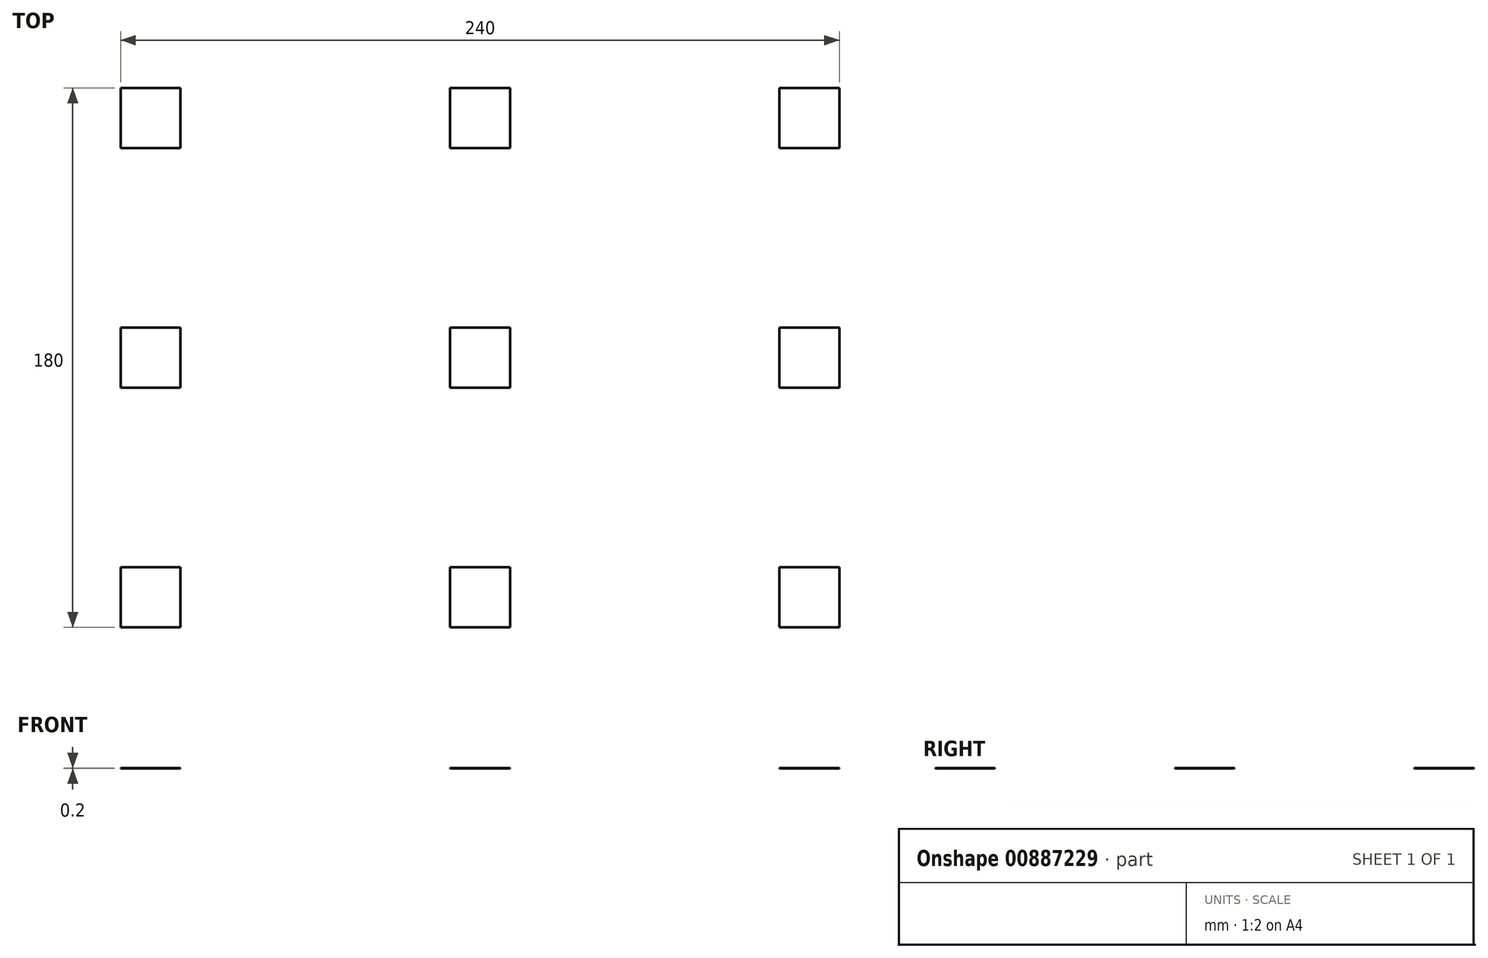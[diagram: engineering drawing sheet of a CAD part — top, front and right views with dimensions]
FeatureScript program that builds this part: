
annotation { "Feature Type Name" : "Feature", "Feature Type Description" : "" }
export const myFeature = defineFeature(function(context is Context, id is Id, definition is map)
    precondition{}
    {
        {
            var Q0;
            Q0=qCreatedBy(makeId("Top.planeOp"), FACE);
            var sketch = newSketch(context, id + "F0", { "sketchPlane" : qUnion([Q0])});
            skLineSegment(sketch, "E0.bottom", {"start": v(10, -10) * mm, "end": v(-10, -10) * mm});
            skLineSegment(sketch, "E0.top", {"start": v(10, 10) * mm, "end": v(-10, 10) * mm});
            skLineSegment(sketch, "E0.left", {"start": v(10, -10) * mm, "end": v(10, 10) * mm});
            skLineSegment(sketch, "E0.right", {"start": v(-10, -10) * mm, "end": v(-10, 10) * mm});
            skPoint(sketch, "E0.middle", {"position": v(0, 0) * mm});
            skLineSegment(sketch, "E1.0.0.1", {"start": v(10, 90) * mm, "end": v(-10, 90) * mm});
            skLineSegment(sketch, "E1.1.0.1", {"start": v(10, 70) * mm, "end": v(10, 90) * mm});
            skLineSegment(sketch, "E1.2.0.1", {"start": v(-10, 70) * mm, "end": v(-10, 90) * mm});
            skPoint(sketch, "E1.3.0.1", {"position": v(0, 80) * mm});
            skLineSegment(sketch, "E1.4.0.1", {"start": v(10, 70) * mm, "end": v(-10, 70) * mm});
            skLineSegment(sketch, "E1.0.0.2", {"start": v(10, 170) * mm, "end": v(-10, 170) * mm});
            skLineSegment(sketch, "E1.1.0.2", {"start": v(10, 150) * mm, "end": v(10, 170) * mm});
            skLineSegment(sketch, "E1.2.0.2", {"start": v(-10, 150) * mm, "end": v(-10, 170) * mm});
            skPoint(sketch, "E1.3.0.2", {"position": v(0, 160) * mm});
            skLineSegment(sketch, "E1.4.0.2", {"start": v(10, 150) * mm, "end": v(-10, 150) * mm});
            skLineSegment(sketch, "E1.0.1.0", {"start": v(120, 10) * mm, "end": v(100, 10) * mm});
            skLineSegment(sketch, "E1.1.1.0", {"start": v(120, -10) * mm, "end": v(120, 10) * mm});
            skLineSegment(sketch, "E1.2.1.0", {"start": v(100, -10) * mm, "end": v(100, 10) * mm});
            skPoint(sketch, "E1.3.1.0", {"position": v(110, 0) * mm});
            skLineSegment(sketch, "E1.4.1.0", {"start": v(120, -10) * mm, "end": v(100, -10) * mm});
            skLineSegment(sketch, "E1.0.1.1", {"start": v(120, 90) * mm, "end": v(100, 90) * mm});
            skLineSegment(sketch, "E1.1.1.1", {"start": v(120, 70) * mm, "end": v(120, 90) * mm});
            skLineSegment(sketch, "E1.2.1.1", {"start": v(100, 70) * mm, "end": v(100, 90) * mm});
            skPoint(sketch, "E1.3.1.1", {"position": v(110, 80) * mm});
            skLineSegment(sketch, "E1.4.1.1", {"start": v(120, 70) * mm, "end": v(100, 70) * mm});
            skLineSegment(sketch, "E1.0.1.2", {"start": v(120, 170) * mm, "end": v(100, 170) * mm});
            skLineSegment(sketch, "E1.1.1.2", {"start": v(120, 150) * mm, "end": v(120, 170) * mm});
            skLineSegment(sketch, "E1.2.1.2", {"start": v(100, 150) * mm, "end": v(100, 170) * mm});
            skPoint(sketch, "E1.3.1.2", {"position": v(110, 160) * mm});
            skLineSegment(sketch, "E1.4.1.2", {"start": v(120, 150) * mm, "end": v(100, 150) * mm});
            skLineSegment(sketch, "E1.0.2.0", {"start": v(230, 10) * mm, "end": v(210, 10) * mm});
            skLineSegment(sketch, "E1.1.2.0", {"start": v(230, -10) * mm, "end": v(230, 10) * mm});
            skLineSegment(sketch, "E1.2.2.0", {"start": v(210, -10) * mm, "end": v(210, 10) * mm});
            skPoint(sketch, "E1.3.2.0", {"position": v(220, 0) * mm});
            skLineSegment(sketch, "E1.4.2.0", {"start": v(230, -10) * mm, "end": v(210, -10) * mm});
            skLineSegment(sketch, "E1.0.2.1", {"start": v(230, 90) * mm, "end": v(210, 90) * mm});
            skLineSegment(sketch, "E1.1.2.1", {"start": v(230, 70) * mm, "end": v(230, 90) * mm});
            skLineSegment(sketch, "E1.2.2.1", {"start": v(210, 70) * mm, "end": v(210, 90) * mm});
            skPoint(sketch, "E1.3.2.1", {"position": v(220, 80) * mm});
            skLineSegment(sketch, "E1.4.2.1", {"start": v(230, 70) * mm, "end": v(210, 70) * mm});
            skLineSegment(sketch, "E1.0.2.2", {"start": v(230, 170) * mm, "end": v(210, 170) * mm});
            skLineSegment(sketch, "E1.1.2.2", {"start": v(230, 150) * mm, "end": v(230, 170) * mm});
            skLineSegment(sketch, "E1.2.2.2", {"start": v(210, 150) * mm, "end": v(210, 170) * mm});
            skPoint(sketch, "E1.3.2.2", {"position": v(220, 160) * mm});
            skLineSegment(sketch, "E1.4.2.2", {"start": v(230, 150) * mm, "end": v(210, 150) * mm});
            skLineSegment(sketch, "E1.direction1", {"start": v(-10, -10) * mm, "end": v(100, -10) * mm, "construction": true});
            skLineSegment(sketch, "E1.direction2", {"start": v(-10, -10) * mm, "end": v(-10, 70) * mm, "construction": true});
            skSolve(sketch);
        }
        {
            var Q0;
            Q0 = qSketchRegion(id + "F0", true);
            extrude(context, id + "F1", {"entities" : qUnion([Q0]), "domain" : OperationDomain.MODEL, "flatOperationType" : FlatOperationType.REMOVE, "depth" : 0.2 * mm, "offsetDistance" : 25 * mm});
        }
    });
